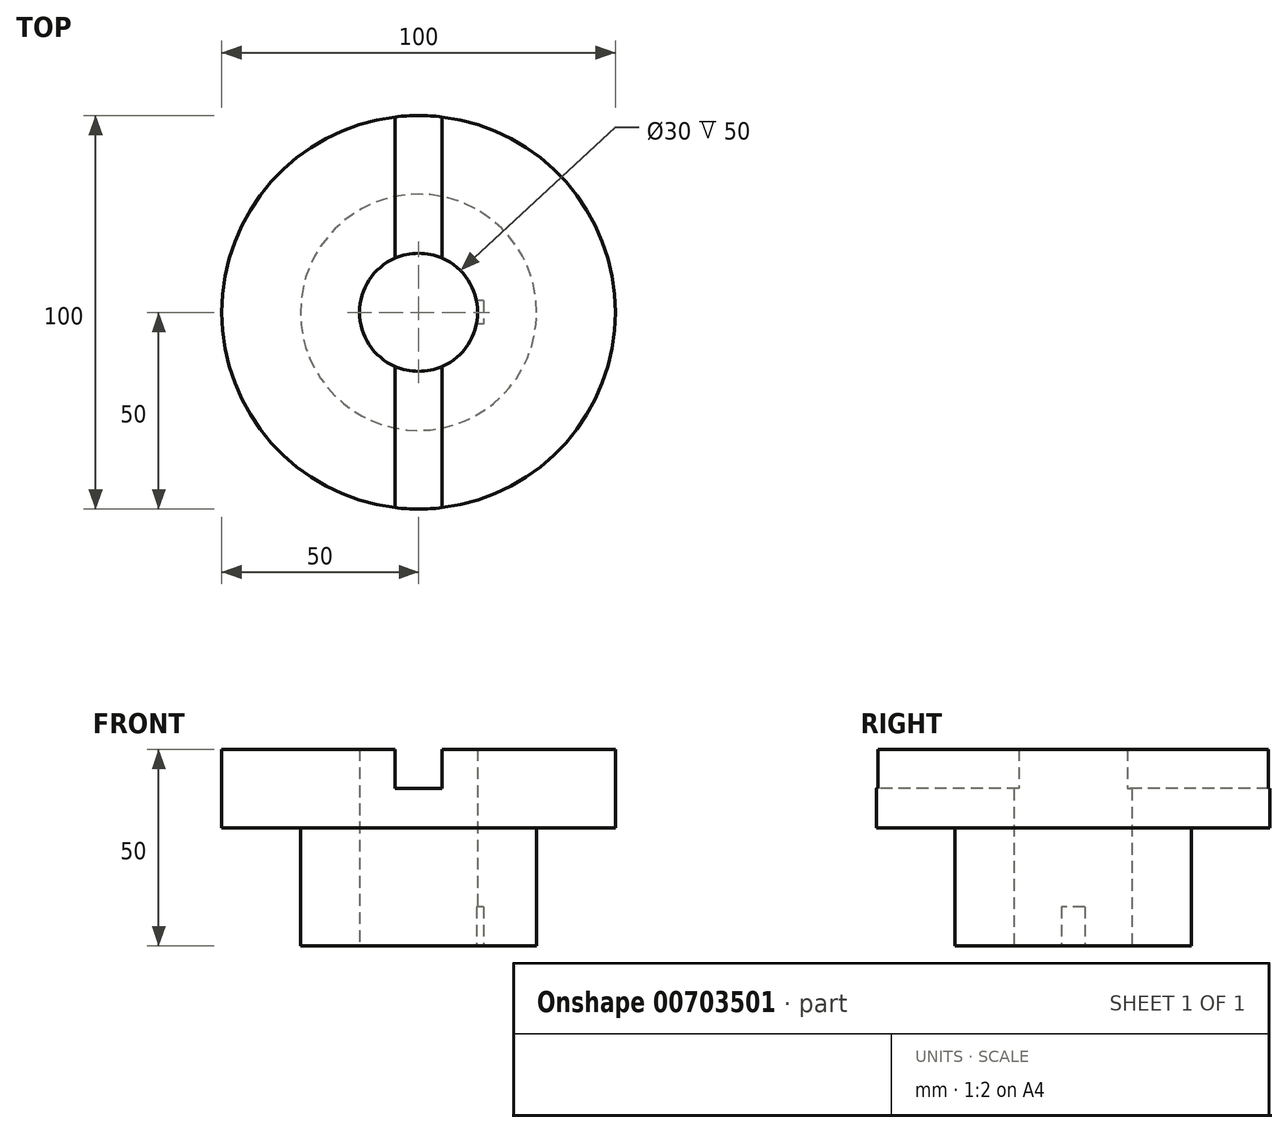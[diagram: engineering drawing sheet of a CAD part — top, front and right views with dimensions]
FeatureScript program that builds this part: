
annotation { "Feature Type Name" : "Feature", "Feature Type Description" : "" }
export const myFeature = defineFeature(function(context is Context, id is Id, definition is map)
    precondition{}
    {
        {
            var Q0;
            Q0=qCreatedBy(makeId("Top.planeOp"),FACE);
            var sketch = newSketch(context, id + "F0", { "sketchPlane" : qUnion([Q0])});
            skCircle(sketch, "E0", {"center": v(0, 0) * mm, "radius": 50 * mm});
            skSolve(sketch);
        }
        {
            var Q0;
            Q0 = qSketchRegion(id + "F0", true);
            extrude(context, id + "F1", {"entities" : qUnion([Q0]), "depth" : 20 * mm, "offsetDistance" : 25 * mm});
        }
        {
            var Q0;
            Q0=makeQuery(id+"F1.opExtrude","CAP_FACE",FACE,{"disambiguationData":[OSD([sQuery(id+"F0.wireOp",EDGE,"E0")])],"isStart":false});
            var sketch = newSketch(context, id + "F2", { "sketchPlane" : qUnion([Q0])});
            skLineSegment(sketch, "E1.bottom", {"start": v(6, 65.4) * mm, "end": v(-6, 65.4) * mm});
            skLineSegment(sketch, "E1.top", {"start": v(6, -65.4) * mm, "end": v(-6, -65.4) * mm});
            skLineSegment(sketch, "E1.left", {"start": v(6, 65.4) * mm, "end": v(6, -65.4) * mm});
            skLineSegment(sketch, "E1.right", {"start": v(-6, 65.4) * mm, "end": v(-6, -65.4) * mm});
            skPoint(sketch, "E1.middle", {"position": v(0, 0) * mm});
            skSolve(sketch);
        }
        {
            var Q0;
            Q0 = qSketchRegion(id + "F2", true);
            extrude(context, id + "F3", {"entities" : qUnion([Q0]), "operationType" : NewBodyOperationType.REMOVE, "oppositeDirection" : true, "depth" : 10 * mm, "offsetDistance" : 25 * mm});
        }
        {
            var Q0;
            Q0=makeQuery(id+"F1.opExtrude","CAP_FACE",FACE,{"disambiguationData":[OSD([sQuery(id+"F0.wireOp",EDGE,"E0")])],"isStart":true});
            var sketch = newSketch(context, id + "F4", { "sketchPlane" : qUnion([Q0])});
            skCircle(sketch, "E2", {"center": v(0, 0) * mm, "radius": 30 * mm});
            skSolve(sketch);
        }
        {
            var Q0;
            Q0 = qSketchRegion(id + "F4", true);
            extrude(context, id + "F5", {"entities" : qUnion([Q0]), "operationType" : NewBodyOperationType.ADD, "depth" : 30 * mm, "offsetDistance" : 25 * mm});
        }
        {
            var Q0;
            Q0=makeQuery(id+"F5.opExtrude","CAP_FACE",FACE,{"disambiguationData":[OSD([sQuery(id+"F4.wireOp",EDGE,"E2")])],"isStart":false});
            var sketch = newSketch(context, id + "F6", { "sketchPlane" : qUnion([Q0])});
            skCircle(sketch, "E3", {"center": v(0, 0) * mm, "radius": 15 * mm});
            skSolve(sketch);
        }
        {
            var Q0;
            Q0=makeQuery(id+"F6.imprint","IMPRINT",FACE,{"disambiguationData":[TD([[makeQuery(id+"F6.imprint","IMPRINT",EDGE,{"derivedFrom":sQuery(id+"F6.wireOp",EDGE,"E3")}),1.0]])]});
            var sketch = newSketch(context, id + "F7", { "sketchPlane" : qUnion([Q0])});
            skLineSegment(sketch, "E4.bottom", {"start": v(16.5, -3) * mm, "end": v(13.5, -3) * mm});
            skLineSegment(sketch, "E4.top", {"start": v(16.5, 3) * mm, "end": v(13.5, 3) * mm});
            skLineSegment(sketch, "E4.left", {"start": v(16.5, -3) * mm, "end": v(16.5, 3) * mm});
            skLineSegment(sketch, "E4.right", {"start": v(13.5, -3) * mm, "end": v(13.5, 3) * mm});
            skPoint(sketch, "E4.middle", {"position": v(15, 0) * mm});
            skSolve(sketch);
        }
        {
            var Q0;
            Q0 = qSketchRegion(id + "F7", true);
            extrude(context, id + "F8", {"entities" : qUnion([Q0]), "operationType" : NewBodyOperationType.REMOVE, "oppositeDirection" : true, "depth" : 10 * mm, "offsetDistance" : 25 * mm});
        }
        {
            var Q0;
            Q0 = qSketchRegion(id + "F6", true);
            extrude(context, id + "F9", {"entities" : qUnion([Q0]), "operationType" : NewBodyOperationType.REMOVE, "endBound" : BoundingType.THROUGH_ALL, "oppositeDirection" : true, "depth" : 25 * mm, "offsetDistance" : 25 * mm});
        }
    });
